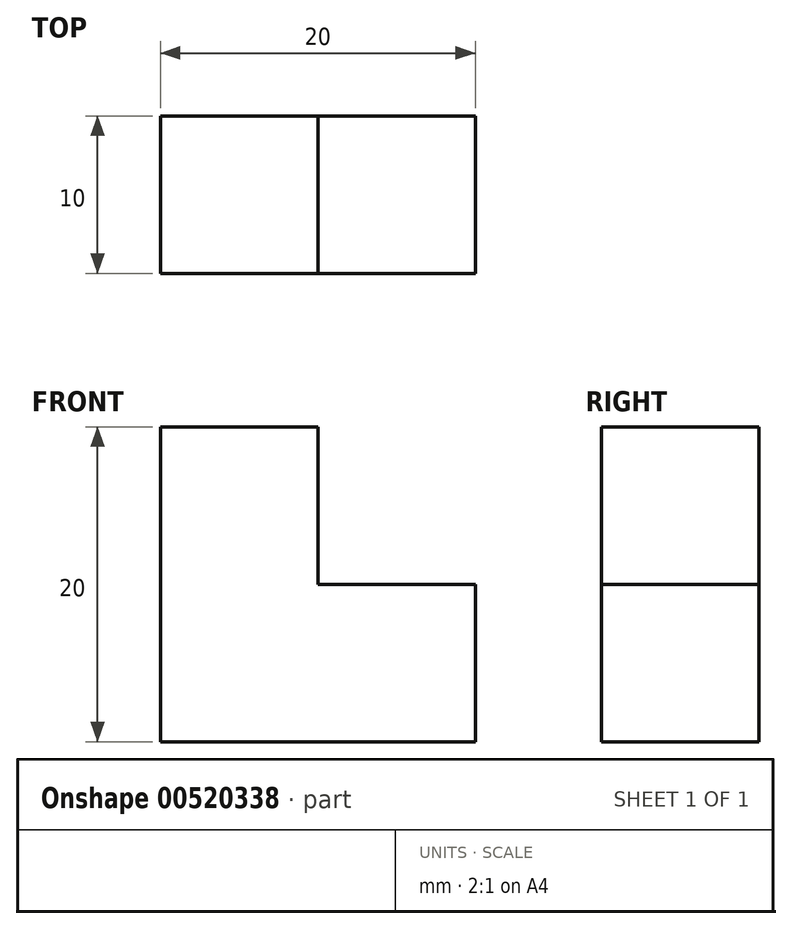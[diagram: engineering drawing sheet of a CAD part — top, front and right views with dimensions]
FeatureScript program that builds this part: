
annotation { "Feature Type Name" : "Feature", "Feature Type Description" : "" }
export const myFeature = defineFeature(function(context is Context, id is Id, definition is map)
    precondition{}
    {
        {
            var Q0;
            Q0=qCreatedBy(makeId("Front.planeOp"),FACE);
            var sketch = newSketch(context, id + "F0", { "sketchPlane" : qUnion([Q0])});
            skLineSegment(sketch, "E0", {"start": v(0, 0) * mm, "end": v(0, 20) * mm});
            skLineSegment(sketch, "E1", {"start": v(0, 20) * mm, "end": v(10, 20) * mm});
            skLineSegment(sketch, "E2", {"start": v(10, 20) * mm, "end": v(10, 10) * mm});
            skLineSegment(sketch, "E3", {"start": v(10, 10) * mm, "end": v(20, 10) * mm});
            skLineSegment(sketch, "E4", {"start": v(20, 10) * mm, "end": v(20, 0) * mm});
            skLineSegment(sketch, "E5", {"start": v(20, 0) * mm, "end": v(0, 0) * mm});
            skSolve(sketch);
        }
        {
            var Q0;
            Q0 = qSketchRegion(id + "F0", true);
            extrude(context, id + "F1", {"entities" : qUnion([Q0]), "depth" : 10 * mm, "offsetDistance" : 25 * mm});
        }
    });
